# Revit family: Haworth_VSeries_Pedestal
name_source: partatom
category: Furniture Systems
revit_build: Autodesk Revit 2018 (Build: 20170223_1515(x64)
units: mm (PartAtom-declared; Revit-internal decimal feet)

## family parameters
Always vertical = Yes
Cut with Voids When Loaded = No
OmniClass Number = 23.40.70.14.64.21
OmniClass Title = Systems Furniture
Part Type = Normal
Room Calculation Point = No
Round Connector Dimension = Use Diameter
Shared = No
Work Plane-Based = No

## types (3) — shared parameters
Actual Depth = 23"
Actual Width = 15"
Assembly Code = E2020200
Attached = Yes
Cabinet Finish = Haworth _ Paint _ Metallic Champagne
Cushion = No
Cushion Finish = Haworth _ Fabric _ Tellure _ Sky 3A-32
Depth = 23"
Description = Haworth - VSeries - Pedestal
Drawer 1 Height = 11 15/16"
Drawer 3 Height = 5 15/16"
Drawer Finish = Haworth _ Paint _ Metallic Champagne
Drawer Three Full Pull = No
Full Pull = No
Manufacturer = Haworth
Max. Depth = 29"
Max. Height = 27 1/2"
Min. Depth = 17"
Min. Height = 21 1/2"
Mobile = No
Model = Haworth - VSeries - Pedestal
Pull Finish = Haworth _ Polymer _ Gray Tone
Revision Number = 2
Size = Verify Final Dim. w/ Haworth
Standard Depths = 17, 23, 29 in
Standard Pull = Yes
Suspended = No
Sustainability Info = http://www.haworth.com
URL = www.haworth.com
URL - Product = http://www.haworth.com
Warranty = http://www.haworth.com

## per-type parameters (varying)
| type | 3 Drawers | Box Box File | Box File | Drawer 2 Height | Drawer Three Standard Pull | File File | Top Location | Total Drawer Height |
| Box Box File - Attached | Yes | Yes | No | 5 15/16" | Yes | No | 27 1/2" | 24 1/8" |
| Box File - Attached | No | No | Yes | 5 15/16" | No | No | 21 1/2" | 18 1/8" |
| File File - Attached | No | No | No | 11 15/16" | No | Yes | 27 1/2" | 24 1/8" |

## geometry (parser evidence)
native form markers: Sweep x11
no freeform markers — native parametric forms only
